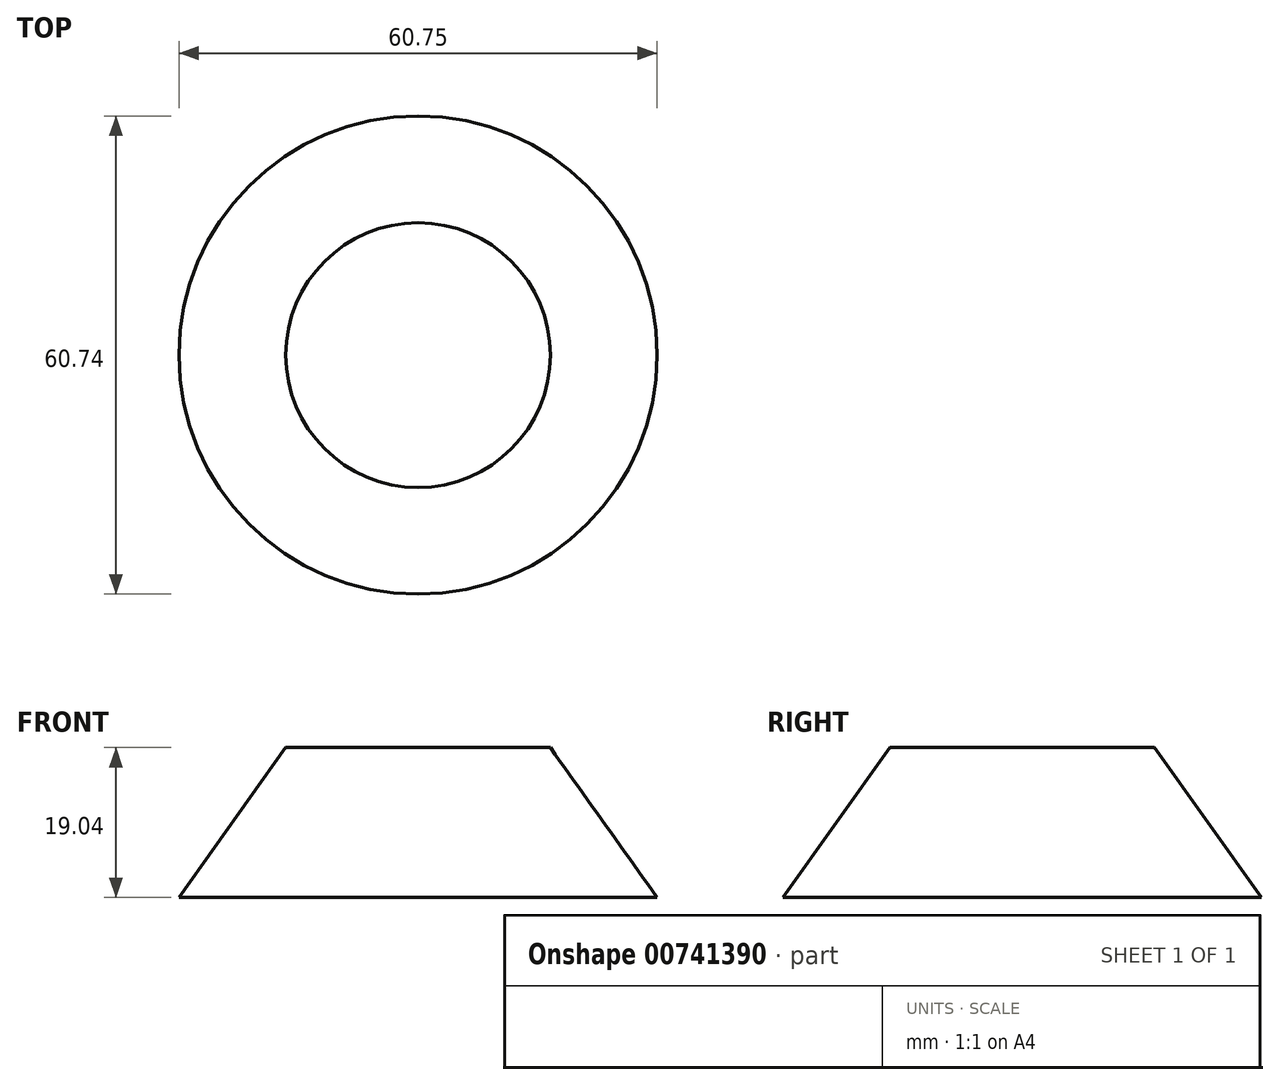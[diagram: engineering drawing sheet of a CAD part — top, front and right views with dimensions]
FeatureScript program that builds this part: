
annotation { "Feature Type Name" : "Feature", "Feature Type Description" : "" }
export const myFeature = defineFeature(function(context is Context, id is Id, definition is map)
    precondition{}
    {
        {
            var Q0;
            Q0=qCreatedBy(makeId("Front.planeOp"),FACE);
            var sketch = newSketch(context, id + "F0", { "sketchPlane" : qUnion([Q0])});
            skLineSegment(sketch, "E0", {"start": v(-2.23, 10.37) * mm, "end": v(-2.23, -8.67) * mm});
            skLineSegment(sketch, "E1", {"start": v(-2.23, -8.67) * mm, "end": v(28.14, -8.67) * mm});
            skLineSegment(sketch, "E2", {"start": v(-2.23, 10.37) * mm, "end": v(14.58, 10.37) * mm});
            skLineSegment(sketch, "E3", {"start": v(14.58, 10.37) * mm, "end": v(28.14, -8.67) * mm});
            skSolve(sketch);
        }
        {
            var Q0;
            Q0=makeQuery(id+"F0.imprint","IMPRINT",FACE,{"disambiguationData":[TD([[makeQuery(id+"F0.imprint","IMPRINT",EDGE,{"derivedFrom":sQuery(id+"F0.wireOp",EDGE,"E0")}),1.0]])]});
            var Q1;
            Q1=sQuery(id+"F0.wireOp",EDGE,"E0");
            revolve(context, id + "F1", {"surfaceOperationType" : NewSurfaceOperationType.NEW, "entities" : qUnion([Q0]), "axis" : qUnion([Q1]), "revolveType" : RevolveType.FULL});
        }
    });
